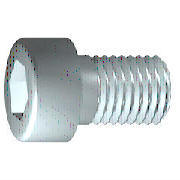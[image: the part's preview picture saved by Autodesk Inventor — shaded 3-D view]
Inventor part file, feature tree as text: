
AUTODESK INVENTOR PART (.ipt)
format: ipt  version: 2020 (Build 240168000, 168)  size: 198,656 bytes
history: native  units: mm (DEFAULTED — no unit token found)
features: sketch x2, other x1, extrude x1, plane x1, fillet x1
ambient origin geometry x7: Origin, YZ Plane, XY Plane, X Axis, Y Axis, Z Axis, Center Point
bodies: Body1 (feature_tree)
feature tree (6):
  other  "Körper"
  extrude  "Loch"  Depth=4.0mm
  plane  "Work Plane1"
  fillet  "Fillet2"  Radius=4.0mm
  sketch  "Skizze1"  dims[d1=7.0mm d2=0.61355mm d3=4.0mm]
  sketch  "Skizze2"  dims[d4=3.0mm d5=60.0deg d6=6.0mm d7=6.0mm d8=4.618802mm d9=10.0mm d10=90.0deg d11=10.0mm d12=0.0mm d13=7.0mm d14=0.0mm d15=0.61345mm d16=0.61345mm d17=0.6mm d19=0.0mm d26=10.0mm d27=45.0deg d28=0.0mm d29=0.0mm d30=0.1mm]
